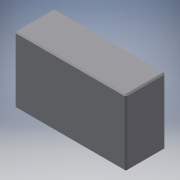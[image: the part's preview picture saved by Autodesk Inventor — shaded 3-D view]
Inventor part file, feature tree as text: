
AUTODESK INVENTOR PART (.ipt)
format: ipt  version: 2018.3 (Build 223284000, 284)  size: 102,912 bytes
history: native  units: mm
features: other x1, extrude x1, chamfer x1, sketch x1
ambient origin geometry x8: Origin, YZ Plane, XZ Plane, XY Plane, X Axis, Y Axis, Z Axis, Center Point
bodies: Body1 (feature_tree)
feature tree (4):
  other  "Bryła1"
  extrude  "Wyciągnięcie proste1"  Depth=15.0mm TaperAngle=0.0deg
  chamfer  "Faza1"  Distance=42.0mm
  sketch  "Szkic1"
